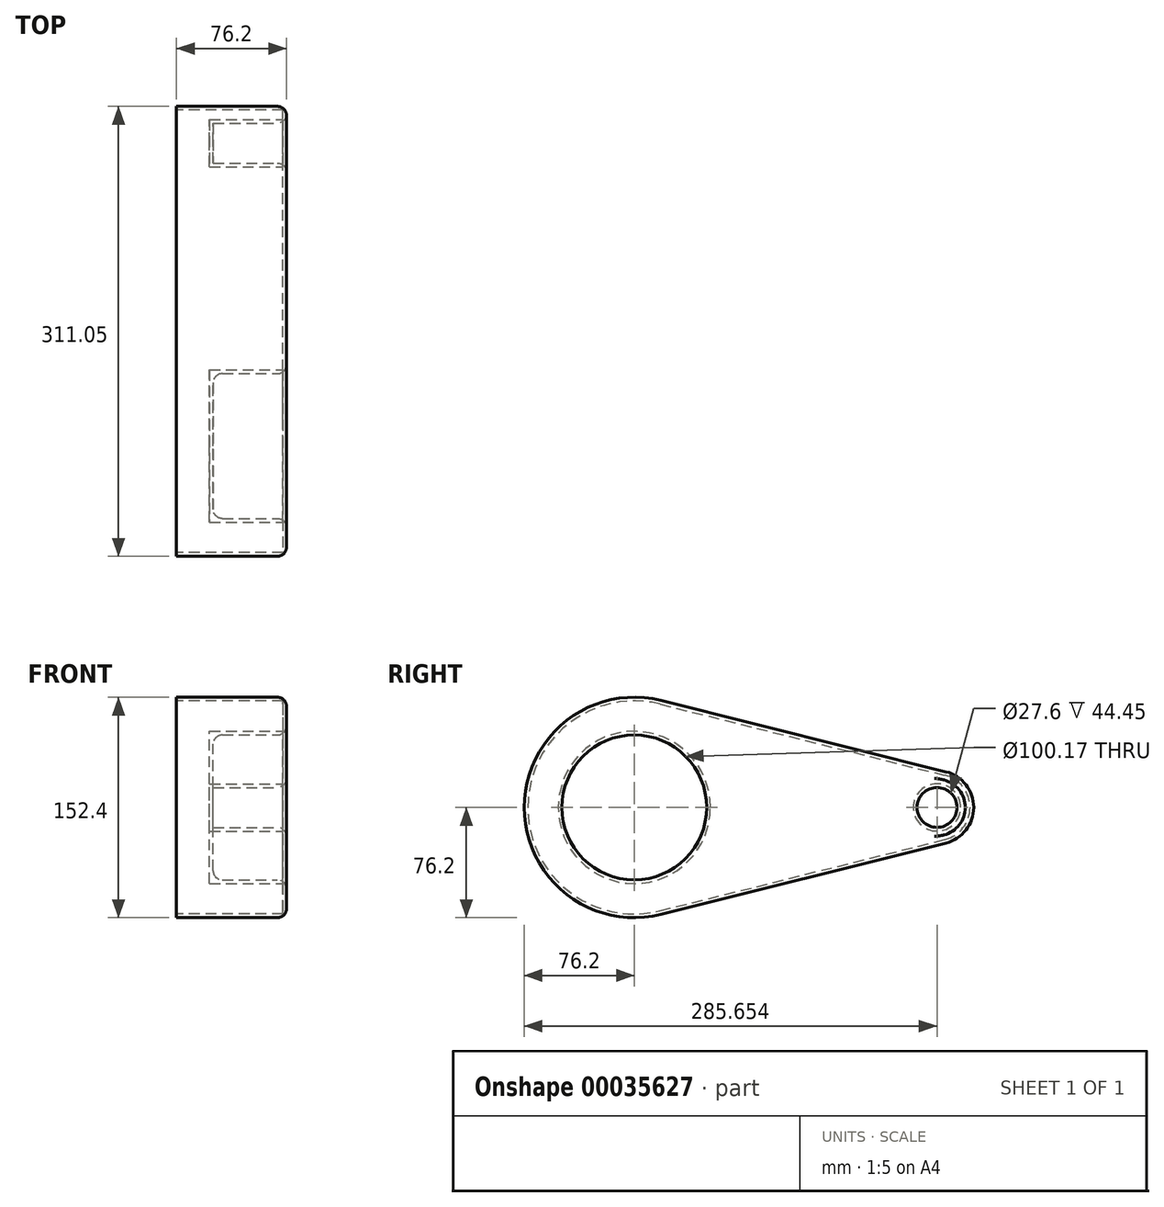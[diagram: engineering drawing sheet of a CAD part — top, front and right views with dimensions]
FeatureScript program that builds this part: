
annotation { "Feature Type Name" : "Feature", "Feature Type Description" : "" }
export const myFeature = defineFeature(function(context is Context, id is Id, definition is map)
    precondition{}
    {
        {
            var Q0;
            Q0=qCreatedBy(makeId("Right.planeOp"),FACE);
            var sketch = newSketch(context, id + "F0", { "sketchPlane" : qUnion([Q0])});
            skCircle(sketch, "E0", {"center": v(0, 0) * mm, "radius": 76.2 * mm});
            skCircle(sketch, "E1", {"center": v(209.45, 0) * mm, "radius": 25.4 * mm});
            skLineSegment(sketch, "E2", {"start": v(18.48, 73.92) * mm, "end": v(215.61, 24.64) * mm});
            skLineSegment(sketch, "E3", {"start": v(18.48, -73.92) * mm, "end": v(215.61, -24.64) * mm});
            skSolve(sketch);
        }
        {
            var Q0;
            {var subQ0=sQuery(id+"F0.wireOp",EDGE,"E0");var subQ2=makeQuery(id+"F0.imprint","INTERSECT",VERTEX,{"derivedFrom":[subQ0,sQuery(id+"F0.wireOp",EDGE,"E2")]});Q0=makeQuery(id+"F0.imprint","IMPRINT",FACE,{"disambiguationData":[TD([[makeQuery(id+"F0.imprint","IMPRINT",EDGE,{"disambiguationData":[TD([[subQ2,-1.0]])],"derivedFrom":subQ0}),1.0]])]});}
            var Q1;
            {var subQ1=sQuery(id+"F0.wireOp",EDGE,"E2");Q1=makeQuery(id+"F0.imprint","IMPRINT",FACE,{"disambiguationData":[TD([[makeQuery(id+"F0.imprint","IMPRINT",EDGE,{"derivedFrom":subQ1}),-1.0]])]});}
            var Q2;
            {var subQ0=sQuery(id+"F0.wireOp",EDGE,"E1");var subQ2=makeQuery(id+"F0.imprint","INTERSECT",VERTEX,{"derivedFrom":[subQ0,sQuery(id+"F0.wireOp",EDGE,"E2")]});Q2=makeQuery(id+"F0.imprint","IMPRINT",FACE,{"disambiguationData":[TD([[makeQuery(id+"F0.imprint","IMPRINT",EDGE,{"disambiguationData":[TD([[subQ2,-1.0]])],"derivedFrom":subQ0}),1.0]])]});}
            extrude(context, id + "F1", {"entities" : qUnion([Q0, Q1, Q2]), "depth" : 76.2 * mm});
        }
        {
            var Q0;
            Q0=makeQuery(id+"F1.opExtrude","CAP_FACE",FACE,{"disambiguationData":[OSD([sQuery(id+"F0.wireOp",EDGE,"E0"),sQuery(id+"F0.wireOp",EDGE,"E1"),sQuery(id+"F0.wireOp",EDGE,"E2"),sQuery(id+"F0.wireOp",EDGE,"E3")])],"isStart":false});
            var sketch = newSketch(context, id + "F2", { "sketchPlane" : qUnion([Q0])});
            skCircle(sketch, "E4", {"center": v(0, 0) * mm, "radius": 50.08 * mm});
            skCircle(sketch, "E5", {"center": v(209.45, 0) * mm, "radius": 13.8 * mm});
            skSolve(sketch);
        }
        {
            var Q0;
            Q0=makeQuery(id+"F2.imprint","IMPRINT",FACE,{"disambiguationData":[TD([[makeQuery(id+"F2.imprint","IMPRINT",EDGE,{"derivedFrom":sQuery(id+"F2.wireOp",EDGE,"E4")}),1.0]])]});
            var Q1;
            Q1=makeQuery(id+"F2.imprint","IMPRINT",FACE,{"disambiguationData":[TD([[makeQuery(id+"F2.imprint","IMPRINT",EDGE,{"derivedFrom":sQuery(id+"F2.wireOp",EDGE,"E5")}),1.0]])]});
            extrude(context, id + "F3", {"entities" : qUnion([Q0, Q1]), "operationType" : NewBodyOperationType.REMOVE, "oppositeDirection" : true, "depth" : 50.8 * mm});
        }
        {
            var Q0;
            Q0=makeQuery(id+"F1.opExtrude","CAP_FACE",FACE,{"disambiguationData":[OSD([sQuery(id+"F0.wireOp",EDGE,"E0"),sQuery(id+"F0.wireOp",EDGE,"E1"),sQuery(id+"F0.wireOp",EDGE,"E2"),sQuery(id+"F0.wireOp",EDGE,"E3")])],"isStart":true});
            shell(context, id + "F4", {"entities" : qUnion([Q0]), "thickness" : 2.54 * mm});
        }
        {
            var Q0;
            Q0=makeQuery(id+"F1.opExtrude","CAP_FACE",FACE,{"disambiguationData":[OSD([sQuery(id+"F0.wireOp",EDGE,"E0"),sQuery(id+"F0.wireOp",EDGE,"E1"),sQuery(id+"F0.wireOp",EDGE,"E2"),sQuery(id+"F0.wireOp",EDGE,"E3")])],"isStart":false});
            var Q1;
            Q1=makeQuery(id+"F3.boolean.opBoolean","COPY",EDGE,{"derivedFrom":makeQuery(id+"F3.opExtrude","CAP_EDGE",EDGE,{"disambiguationData":[OSD([sQuery(id+"F2.wireOp",EDGE,"E4")])],"isStart":false})});
            var Q2;
            Q2=makeQuery(id+"F3.boolean.opBoolean","COPY",EDGE,{"derivedFrom":makeQuery(id+"F3.opExtrude","CAP_EDGE",EDGE,{"disambiguationData":[OSD([sQuery(id+"F2.wireOp",EDGE,"E5")])],"isStart":true})});
            fillet(context, id + "F5", {"entities" : qUnion([Q0, Q1, Q2]), "radius" : 6.35 * mm, "tangentPropagation" : true, "allowEdgeOverflow" : false});
        }
    });
